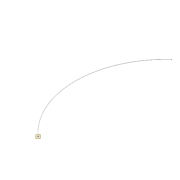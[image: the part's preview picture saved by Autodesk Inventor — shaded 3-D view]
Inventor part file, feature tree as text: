
AUTODESK INVENTOR PART (.ipt)
format: ipt  version: 2022 (Build 260153000, 153)  size: 82,944 bytes
history: native  units: mm
features: sketch x2, plane x1, sweep x1
ambient origin geometry x8: Origin, YZ Plane, XZ Plane, XY Plane, X Axis, Y Axis, Z Axis, Center Point
bodies: Solid1 (feature_tree)
feature tree (4):
  sketch  "Sketch1"  dims[d4=888.0mm d5=600.0mm]
  plane  "Work Plane1"
  sweep  "Sweep1"
  sketch  "Sketch2"  dims[d6=4.0mm d7=0.0mm d8=0.0mm]
